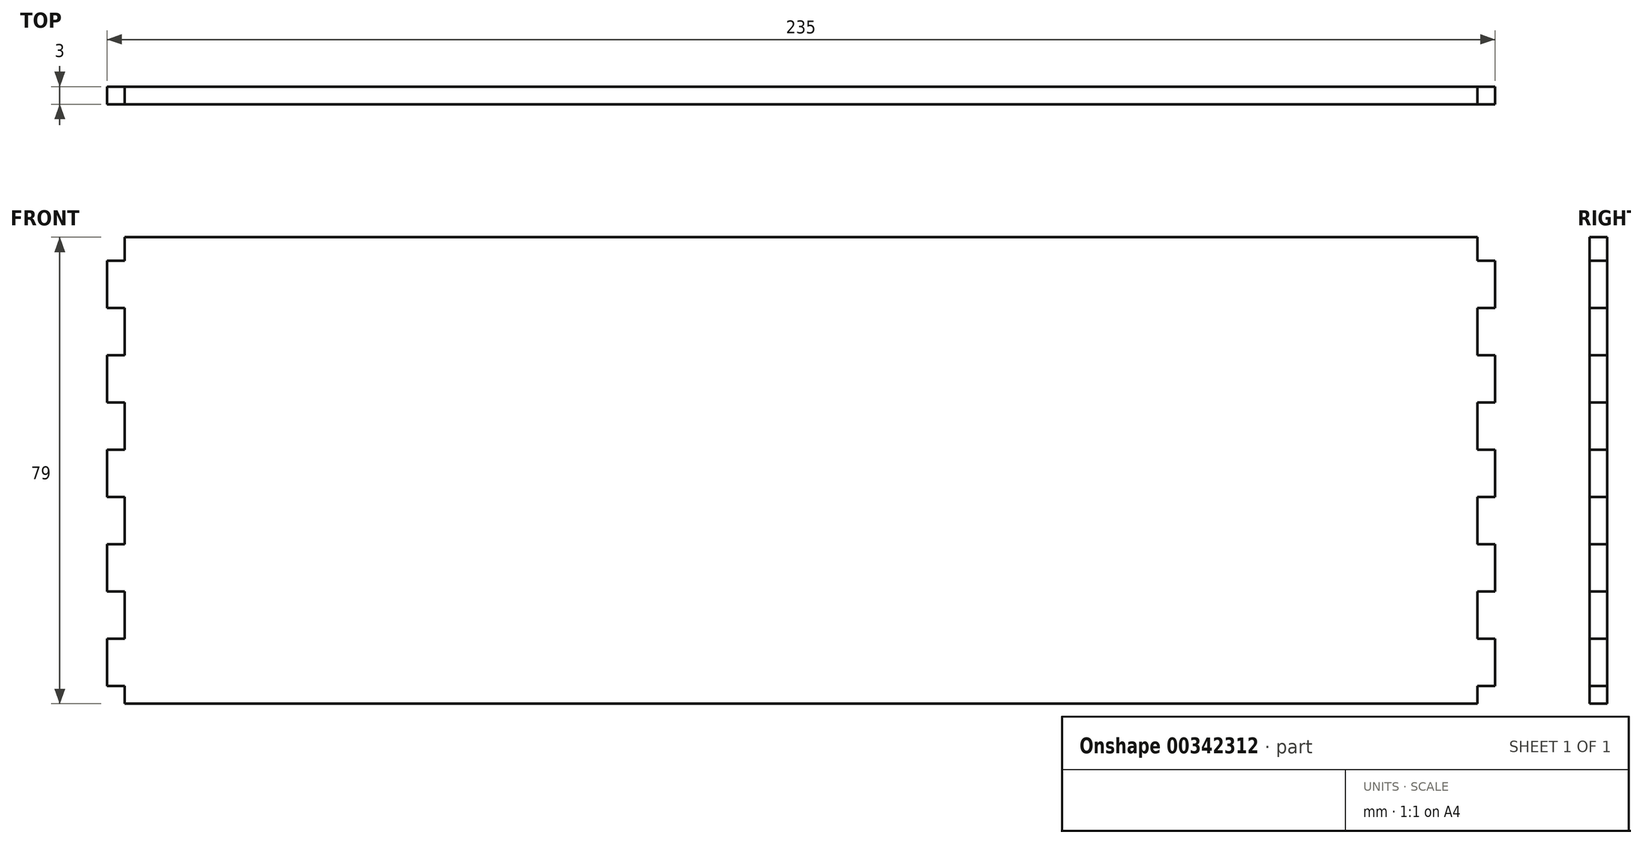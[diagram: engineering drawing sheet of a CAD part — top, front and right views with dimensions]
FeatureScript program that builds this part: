
annotation { "Feature Type Name" : "Feature", "Feature Type Description" : "" }
export const myFeature = defineFeature(function(context is Context, id is Id, definition is map)
    precondition{}
    {
        {
            var Q0;
            Q0=qCreatedBy(makeId("Front.planeOp"),FACE);
            var sketch = newSketch(context, id + "F0", { "sketchPlane" : qUnion([Q0])});
            skLineSegment(sketch, "E0.bottom", {"start": v(0, 0) * mm, "end": v(229, 0) * mm});
            skLineSegment(sketch, "E0.top", {"start": v(0, 79) * mm, "end": v(229, 79) * mm});
            skLineSegment(sketch, "E1", {"start": v(0, 59) * mm, "end": v(-3, 59) * mm});
            skLineSegment(sketch, "E2", {"start": v(-3, 59) * mm, "end": v(-3, 51) * mm});
            skLineSegment(sketch, "E3", {"start": v(-3, 51) * mm, "end": v(0, 51) * mm});
            skLineSegment(sketch, "E4", {"start": v(0, 51) * mm, "end": v(0, 43) * mm});
            skLineSegment(sketch, "E5", {"start": v(0, 43) * mm, "end": v(-3, 43) * mm});
            skLineSegment(sketch, "E6", {"start": v(-3, 43) * mm, "end": v(-3, 35) * mm});
            skLineSegment(sketch, "E7", {"start": v(-3, 35) * mm, "end": v(0, 35) * mm});
            skLineSegment(sketch, "E8", {"start": v(229, 43) * mm, "end": v(232, 43) * mm});
            skLineSegment(sketch, "E9", {"start": v(232, 43) * mm, "end": v(232, 35) * mm});
            skLineSegment(sketch, "E10", {"start": v(232, 35) * mm, "end": v(229, 35) * mm});
            skLineSegment(sketch, "E11", {"start": v(229, 35) * mm, "end": v(229, 27) * mm});
            skLineSegment(sketch, "E12", {"start": v(229, 27) * mm, "end": v(232, 27) * mm});
            skLineSegment(sketch, "E13", {"start": v(232, 27) * mm, "end": v(232, 19) * mm});
            skLineSegment(sketch, "E14", {"start": v(232, 19) * mm, "end": v(229, 19) * mm});
            skLineSegment(sketch, "E15", {"start": v(0, 59) * mm, "end": v(0, 67) * mm});
            skLineSegment(sketch, "E16", {"start": v(0, 67) * mm, "end": v(-3, 67) * mm});
            skLineSegment(sketch, "E17", {"start": v(-3, 67) * mm, "end": v(-3, 75) * mm});
            skLineSegment(sketch, "E18", {"start": v(-3, 75) * mm, "end": v(0, 75) * mm});
            skLineSegment(sketch, "E19", {"start": v(0, 75) * mm, "end": v(0, 79) * mm});
            skLineSegment(sketch, "E20", {"start": v(0, 35) * mm, "end": v(0, 27) * mm});
            skLineSegment(sketch, "E21", {"start": v(0, 27) * mm, "end": v(-3, 27) * mm});
            skLineSegment(sketch, "E22", {"start": v(-3, 27) * mm, "end": v(-3, 19) * mm});
            skLineSegment(sketch, "E23", {"start": v(-3, 19) * mm, "end": v(0, 19) * mm});
            skLineSegment(sketch, "E24", {"start": v(0, 19) * mm, "end": v(0, 11) * mm});
            skLineSegment(sketch, "E25", {"start": v(0, 11) * mm, "end": v(-3, 11) * mm});
            skLineSegment(sketch, "E26", {"start": v(-3, 11) * mm, "end": v(-3, 3) * mm});
            skLineSegment(sketch, "E27", {"start": v(-3, 3) * mm, "end": v(0, 3) * mm});
            skLineSegment(sketch, "E28", {"start": v(0, 3) * mm, "end": v(0, 0) * mm});
            skLineSegment(sketch, "E29", {"start": v(229, 79) * mm, "end": v(229, 75) * mm});
            skLineSegment(sketch, "E30", {"start": v(229, 75) * mm, "end": v(232, 75) * mm});
            skLineSegment(sketch, "E31", {"start": v(232, 75) * mm, "end": v(232, 67) * mm});
            skLineSegment(sketch, "E32", {"start": v(232, 67) * mm, "end": v(229, 67) * mm});
            skLineSegment(sketch, "E33", {"start": v(229, 67) * mm, "end": v(229, 59) * mm});
            skLineSegment(sketch, "E34", {"start": v(229, 59) * mm, "end": v(232, 59) * mm});
            skLineSegment(sketch, "E35", {"start": v(232, 59) * mm, "end": v(232, 51) * mm});
            skLineSegment(sketch, "E36", {"start": v(232, 51) * mm, "end": v(229, 51) * mm});
            skLineSegment(sketch, "E37", {"start": v(229, 51) * mm, "end": v(229, 43) * mm});
            skLineSegment(sketch, "E38", {"start": v(229, 19) * mm, "end": v(229, 11) * mm});
            skLineSegment(sketch, "E39", {"start": v(229, 11) * mm, "end": v(232, 11) * mm});
            skLineSegment(sketch, "E40", {"start": v(232, 11) * mm, "end": v(232, 3) * mm});
            skLineSegment(sketch, "E41", {"start": v(232, 3) * mm, "end": v(229, 3) * mm});
            skLineSegment(sketch, "E42", {"start": v(229, 3) * mm, "end": v(229, 0) * mm});
            skSolve(sketch);
        }
        {
            var Q0;
            Q0 = qSketchRegion(id + "F0", true);
            extrude(context, id + "F1", {"entities" : qUnion([Q0]), "depth" : 3 * mm, "offsetDistance" : 25 * mm});
        }
    });
